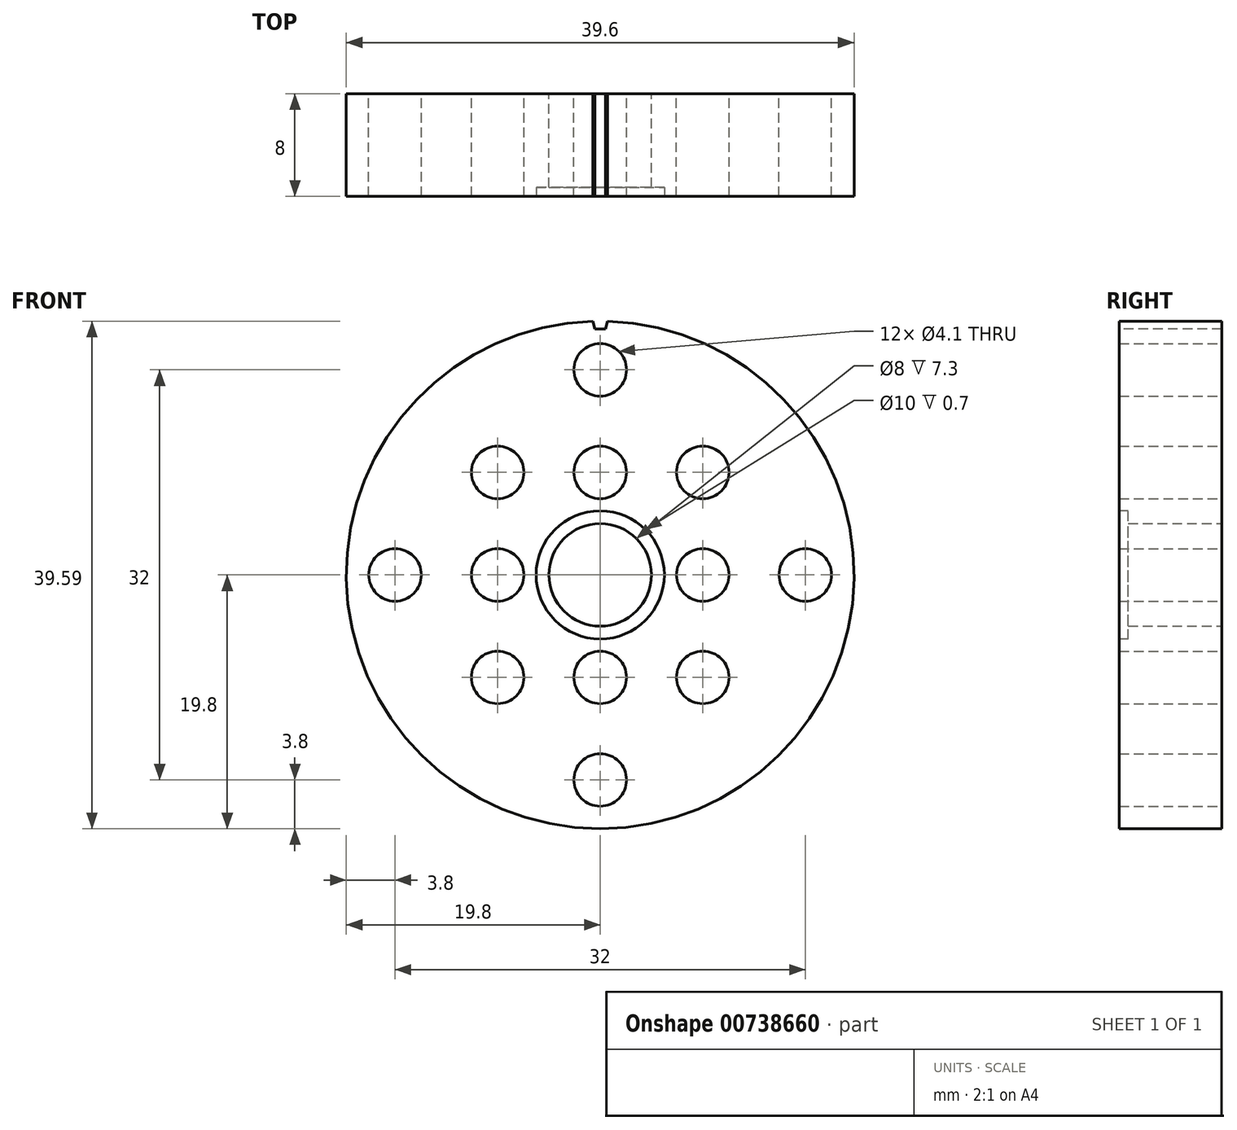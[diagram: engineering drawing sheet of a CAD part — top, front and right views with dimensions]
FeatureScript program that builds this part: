
annotation { "Feature Type Name" : "Feature", "Feature Type Description" : "" }
export const myFeature = defineFeature(function(context is Context, id is Id, definition is map)
    precondition{}
    {
        {
            var Q0;
            Q0=qCreatedBy(makeId("Front.planeOp"),FACE);
            var sketch = newSketch(context, id + "F0", { "sketchPlane" : qUnion([Q0])});
            skCircle(sketch, "E0", {"center": v(0, 0) * mm, "radius": 19.8 * mm});
            skCircle(sketch, "E1", {"center": v(-16, 0) * mm, "radius": 2.05 * mm});
            skCircle(sketch, "E2", {"center": v(-8, 0) * mm, "radius": 2.05 * mm});
            skCircle(sketch, "E3", {"center": v(-8, 8) * mm, "radius": 2.05 * mm});
            skCircle(sketch, "E4", {"center": v(0, 16) * mm, "radius": 2.05 * mm});
            skCircle(sketch, "E5", {"center": v(0, 8) * mm, "radius": 2.05 * mm});
            skCircle(sketch, "E6.MirrorC", {"center": v(8, 0) * mm, "radius": 2.05 * mm});
            skCircle(sketch, "E7.MirrorC", {"center": v(8, 8) * mm, "radius": 2.05 * mm});
            skCircle(sketch, "E8.MirrorC", {"center": v(16, 0) * mm, "radius": 2.05 * mm});
            skCircle(sketch, "E9.MirrorC", {"center": v(-8, -8) * mm, "radius": 2.05 * mm});
            skCircle(sketch, "E10.MirrorC", {"center": v(0, -8) * mm, "radius": 2.05 * mm});
            skCircle(sketch, "E11.MirrorC", {"center": v(8, -8) * mm, "radius": 2.05 * mm});
            skCircle(sketch, "E12.MirrorC", {"center": v(0, -16) * mm, "radius": 2.05 * mm});
            skCircle(sketch, "E13", {"center": v(0, 0) * mm, "radius": 4 * mm});
            skSolve(sketch);
        }
        {
            var Q0;
            Q0=makeQuery(id+"F0.imprint","IMPRINT",FACE,{"disambiguationData":[TD([[makeQuery(id+"F0.imprint","IMPRINT",EDGE,{"derivedFrom":sQuery(id+"F0.wireOp",EDGE,"E0")}),1.0]])]});
            extrude(context, id + "F1", {"entities" : qUnion([Q0]), "endBound" : BoundingType.SYMMETRIC, "depth" : 8 * mm, "offsetDistance" : 25.4 * mm});
        }
        {
            var Q0;
            Q0=makeQuery(id+"F1.opExtrude","CAP_FACE",FACE,{"disambiguationData":[OSD([sQuery(id+"F0.wireOp",EDGE,"E0"),sQuery(id+"F0.wireOp",EDGE,"E1"),sQuery(id+"F0.wireOp",EDGE,"E2"),sQuery(id+"F0.wireOp",EDGE,"E3"),sQuery(id+"F0.wireOp",EDGE,"E4"),sQuery(id+"F0.wireOp",EDGE,"E5"),sQuery(id+"F0.wireOp",EDGE,"E6.MirrorC"),sQuery(id+"F0.wireOp",EDGE,"E7.MirrorC"),sQuery(id+"F0.wireOp",EDGE,"E8.MirrorC"),sQuery(id+"F0.wireOp",EDGE,"E9.MirrorC"),sQuery(id+"F0.wireOp",EDGE,"E10.MirrorC"),sQuery(id+"F0.wireOp",EDGE,"E11.MirrorC"),sQuery(id+"F0.wireOp",EDGE,"E12.MirrorC"),sQuery(id+"F0.wireOp",EDGE,"E13")])],"isStart":false});
            var sketch = newSketch(context, id + "F2", { "sketchPlane" : qUnion([Q0])});
            skCircle(sketch, "E14", {"center": v(0, 0) * mm, "radius": 5 * mm});
            skSolve(sketch);
        }
        {
            var Q0;
            Q0 = qSketchRegion(id + "F2", true);
            extrude(context, id + "F3", {"entities" : qUnion([Q0]), "operationType" : NewBodyOperationType.REMOVE, "oppositeDirection" : true, "depth" : .7 * mm, "offsetDistance" : 25.4 * mm});
        }
        {
            var Q0;
            Q0=makeQuery(id+"F1.opExtrude","CAP_FACE",FACE,{"disambiguationData":[OSD([sQuery(id+"F0.wireOp",EDGE,"E0"),sQuery(id+"F0.wireOp",EDGE,"E1"),sQuery(id+"F0.wireOp",EDGE,"E2"),sQuery(id+"F0.wireOp",EDGE,"E3"),sQuery(id+"F0.wireOp",EDGE,"E4"),sQuery(id+"F0.wireOp",EDGE,"E5"),sQuery(id+"F0.wireOp",EDGE,"E6.MirrorC"),sQuery(id+"F0.wireOp",EDGE,"E7.MirrorC"),sQuery(id+"F0.wireOp",EDGE,"E8.MirrorC"),sQuery(id+"F0.wireOp",EDGE,"E9.MirrorC"),sQuery(id+"F0.wireOp",EDGE,"E10.MirrorC"),sQuery(id+"F0.wireOp",EDGE,"E11.MirrorC"),sQuery(id+"F0.wireOp",EDGE,"E12.MirrorC"),sQuery(id+"F0.wireOp",EDGE,"E13")])],"isStart":false});
            var sketch = newSketch(context, id + "F4", { "sketchPlane" : qUnion([Q0])});
            skLineSegment(sketch, "E15", {"start": v(-1.08, 21.74) * mm, "end": v(-0.4, 19.2) * mm});
            skLineSegment(sketch, "E16", {"start": v(0.4, 19.2) * mm, "end": v(1.08, 21.74) * mm});
            skLineSegment(sketch, "E17", {"start": v(1.08, 21.74) * mm, "end": v(-1.08, 21.74) * mm});
            skArc(sketch, "E18", {"start": v(0.4, 19.2) * mm, "mid": v(0, 19.2) * mm, "end": v(-0.4, 19.2) * mm});
            skSolve(sketch);
        }
        {
            var Q0;
            Q0 = qSketchRegion(id + "F4", true);
            extrude(context, id + "F5", {"entities" : qUnion([Q0]), "operationType" : NewBodyOperationType.REMOVE, "oppositeDirection" : true, "depth" : 25.4 * mm, "offsetDistance" : 25.4 * mm});
        }
    });
